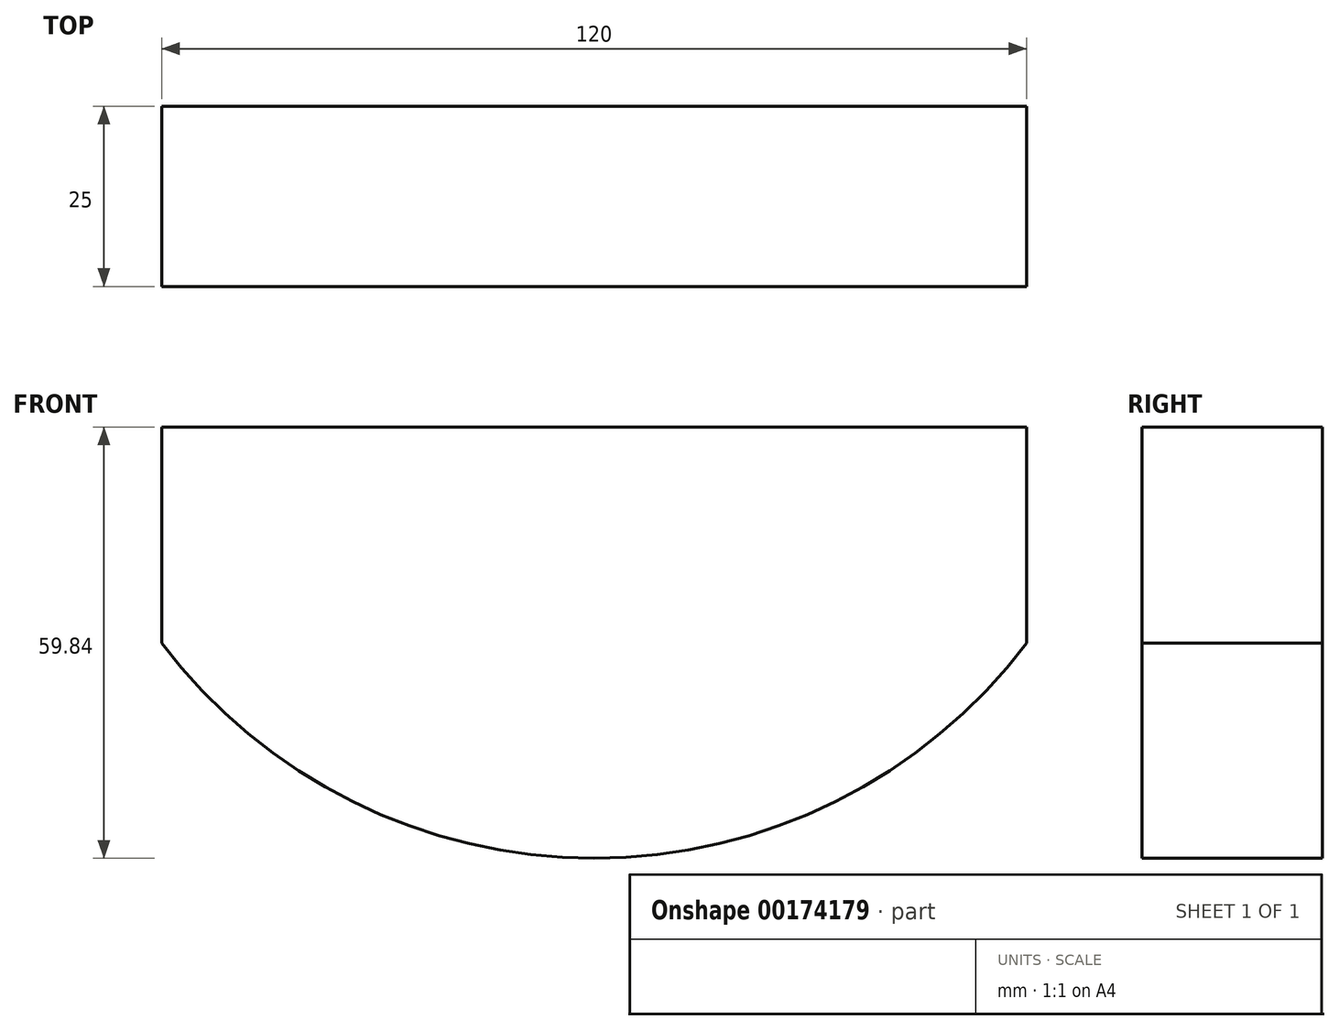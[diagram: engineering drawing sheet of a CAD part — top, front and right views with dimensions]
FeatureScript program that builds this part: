
annotation { "Feature Type Name" : "Feature", "Feature Type Description" : "" }
export const myFeature = defineFeature(function(context is Context, id is Id, definition is map)
    precondition{}
    {
        {
            var Q0;
            Q0=qCreatedBy(makeId("Front.planeOp"),FACE);
            var sketch = newSketch(context, id + "F0", { "sketchPlane" : qUnion([Q0])});
            skLineSegment(sketch, "E0.bottom", {"start": v(-60, 30) * mm, "end": v(60, 30) * mm});
            skLineSegment(sketch, "E0.left", {"start": v(-60, 30) * mm, "end": v(-60, 0) * mm});
            skLineSegment(sketch, "E0.right", {"start": v(60, 30) * mm, "end": v(60, 0) * mm});
            skArc(sketch, "E1", {"start": v(-60, 0) * mm, "mid": v(0, -29.84) * mm, "end": v(60, 0) * mm});
            skPoint(sketch, "E0.top.start.orphan", {"position": v(-60, -30) * mm});
            skPoint(sketch, "E2.orphan", {"position": v(60, -30) * mm});
            skSolve(sketch);
        }
        {
            var Q0;
            Q0=makeQuery(id+"F0.imprint","IMPRINT",FACE,{"disambiguationData":[TD([[makeQuery(id+"F0.imprint","IMPRINT",EDGE,{"derivedFrom":sQuery(id+"F0.wireOp",EDGE,"E0.bottom")}),-1.0]])]});
            extrude(context, id + "F1", {"entities" : qUnion([Q0]), "depth" : 25 * mm});
        }
    });
